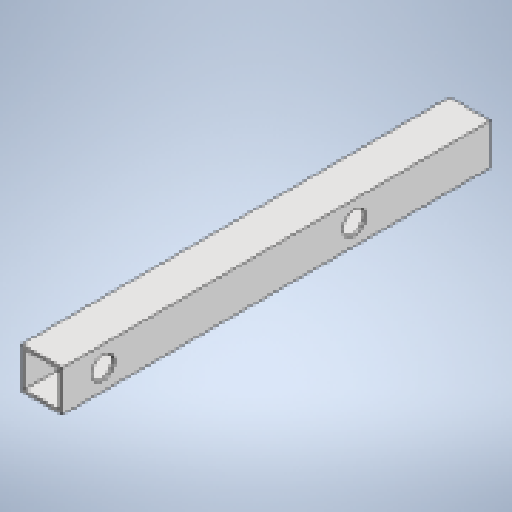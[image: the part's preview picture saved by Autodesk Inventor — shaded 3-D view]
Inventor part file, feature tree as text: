
AUTODESK INVENTOR PART (.ipt)
format: ipt  version: 2025.1 (Build 291241020, 241B)  size: 192,512 bytes
history: native  units: mm
features: extrude x2, sketch x2, projected_geometry x1
ambient origin geometry x8: Origin, YZ Plane, XZ Plane, XY Plane, X Axis, Y Axis, Z Axis, Center Point
bodies: Body1 (feature_tree)
feature tree (5):
  extrude  "Extrusion3"  Depth=30.0mm
  extrude  "Extrusion4"  Depth=2.0mm
  sketch  "Sketch9"  dims[d61=500.0mm d172=30.0mm]
  sketch  "Sketch10"  dims[d173=30.0mm d174=2.0mm d175=315.0mm d176=0.0mm d177=17.0mm d178=17.0mm d179=0.0mm d180=0.0mm d181=30.0mm d182=130.0mm d183=315.0mm d184=435.0mm d185=500.0mm d186=17.0mm]
  projected_geometry  "Projected Loop3"
